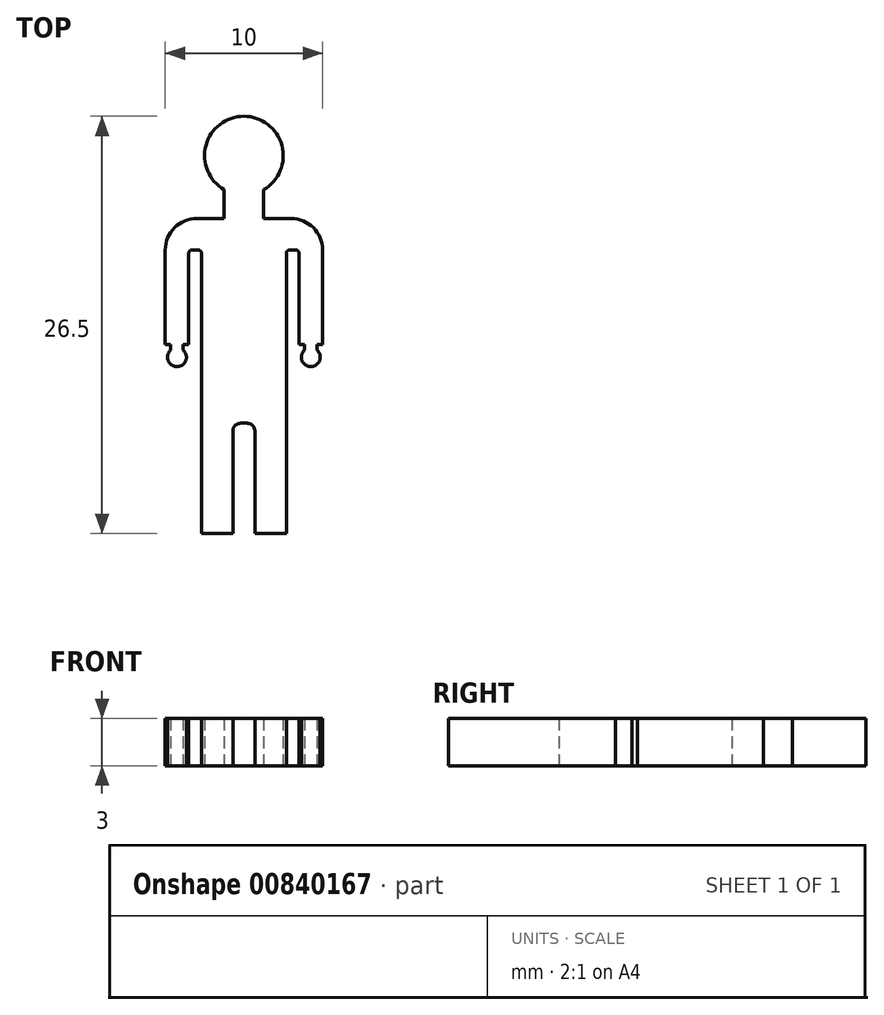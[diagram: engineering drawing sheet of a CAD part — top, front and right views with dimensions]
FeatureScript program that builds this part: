
annotation { "Feature Type Name" : "Feature", "Feature Type Description" : "" }
export const myFeature = defineFeature(function(context is Context, id is Id, definition is map)
    precondition{}
    {
        {
            var Q0;
            Q0=qCreatedBy(makeId("Top.planeOp"),FACE);
            var sketch = newSketch(context, id + "F0", { "sketchPlane" : qUnion([Q0])});
            skArc(sketch, "E0", {"start": v(1.25, -2.17) * mm, "mid": v(0, 2.5) * mm, "end": v(-1.25, -2.17) * mm});
            skLineSegment(sketch, "E1", {"start": v(-1.25, -4) * mm, "end": v(-3, -4) * mm});
            skLineSegment(sketch, "E2", {"start": v(-5, -6) * mm, "end": v(-5, -12) * mm});
            skLineSegment(sketch, "E3", {"start": v(-5, -12) * mm, "end": v(-4.65, -12) * mm});
            skLineSegment(sketch, "E4", {"start": v(-3.5, -12) * mm, "end": v(-3.5, -6.2) * mm});
            skLineSegment(sketch, "E5", {"start": v(-3.3, -6) * mm, "end": v(-2.9, -6) * mm});
            skLineSegment(sketch, "E6", {"start": v(-2.7, -6.2) * mm, "end": v(-2.7, -24) * mm});
            skLineSegment(sketch, "E7", {"start": v(-2.7, -24) * mm, "end": v(-0.7, -24) * mm});
            skLineSegment(sketch, "E8", {"start": v(-0.7, -24) * mm, "end": v(-0.7, -17.5) * mm});
            skLineSegment(sketch, "E9", {"start": v(-0.2, -17) * mm, "end": v(0, -17) * mm});
            skLineSegment(sketch, "E10", {"start": v(0, -4) * mm, "end": v(0, -17) * mm});
            skLineSegment(sketch, "E11.MirrorCS", {"start": v(1.25, -4) * mm, "end": v(3, -4) * mm});
            skLineSegment(sketch, "E12.MirrorCS", {"start": v(5, -6) * mm, "end": v(5, -12) * mm});
            skLineSegment(sketch, "E13.MirrorCS", {"start": v(3.5, -12) * mm, "end": v(3.5, -6.2) * mm});
            skLineSegment(sketch, "E14.MirrorCS", {"start": v(5, -12) * mm, "end": v(4.65, -12) * mm});
            skLineSegment(sketch, "E15.MirrorCS", {"start": v(3.3, -6) * mm, "end": v(2.9, -6) * mm});
            skLineSegment(sketch, "E16.MirrorCS", {"start": v(2.7, -6.2) * mm, "end": v(2.7, -24) * mm});
            skLineSegment(sketch, "E17.MirrorCS", {"start": v(2.7, -24) * mm, "end": v(0.7, -24) * mm});
            skLineSegment(sketch, "E18.MirrorCS", {"start": v(0.2, -17) * mm, "end": v(0, -17) * mm});
            skLineSegment(sketch, "E19.MirrorCS", {"start": v(0.7, -24) * mm, "end": v(0.7, -17.5) * mm});
            skLineSegment(sketch, "E20", {"start": v(-1.25, -4) * mm, "end": v(-1.25, -2.17) * mm});
            skLineSegment(sketch, "E21", {"start": v(1.25, -2.17) * mm, "end": v(1.25, -4) * mm});
            skPoint(sketch, "E22.orphan", {"position": v(0, -4) * mm});
            skPoint(sketch, "E23.visualSharp", {"position": v(-5, -4) * mm});
            skArc(sketch, "E23.filletArc", {"start": v(-3, -4) * mm, "mid": v(-4.41, -4.59) * mm, "end": v(-5, -6) * mm});
            skPoint(sketch, "E24.visualSharp", {"position": v(5, -4) * mm});
            skArc(sketch, "E24.filletArc", {"start": v(5, -6) * mm, "mid": v(4.41, -4.59) * mm, "end": v(3, -4) * mm});
            skPoint(sketch, "E25.visualSharp", {"position": v(-3.5, -6) * mm});
            skArc(sketch, "E25.filletArc", {"start": v(-3.3, -6) * mm, "mid": v(-3.44, -6.06) * mm, "end": v(-3.5, -6.2) * mm});
            skPoint(sketch, "E26.visualSharp", {"position": v(-2.7, -6) * mm});
            skArc(sketch, "E26.filletArc", {"start": v(-2.7, -6.2) * mm, "mid": v(-2.76, -6.06) * mm, "end": v(-2.9, -6) * mm});
            skPoint(sketch, "E27.visualSharp", {"position": v(2.7, -6) * mm});
            skArc(sketch, "E27.filletArc", {"start": v(2.9, -6) * mm, "mid": v(2.76, -6.06) * mm, "end": v(2.7, -6.2) * mm});
            skPoint(sketch, "E28.visualSharp", {"position": v(3.5, -6) * mm});
            skArc(sketch, "E28.filletArc", {"start": v(3.5, -6.2) * mm, "mid": v(3.44, -6.06) * mm, "end": v(3.3, -6) * mm});
            skPoint(sketch, "E29.visualSharp", {"position": v(-0.7, -17) * mm});
            skArc(sketch, "E29.filletArc", {"start": v(-0.2, -17) * mm, "mid": v(-0.55, -17.15) * mm, "end": v(-0.7, -17.5) * mm});
            skPoint(sketch, "E30.visualSharp", {"position": v(0.7, -17) * mm});
            skArc(sketch, "E30.filletArc", {"start": v(0.7, -17.5) * mm, "mid": v(0.55, -17.15) * mm, "end": v(0.2, -17) * mm});
            skArc(sketch, "E31", {"start": v(-4.65, -12.36) * mm, "mid": v(-4.25, -13.4) * mm, "end": v(-3.85, -12.36) * mm});
            skLineSegment(sketch, "E32", {"start": v(-4.65, -12) * mm, "end": v(-4.65, -12.36) * mm});
            skLineSegment(sketch, "E33", {"start": v(-3.85, -12.36) * mm, "end": v(-3.85, -12) * mm});
            skLineSegment(sketch, "E34.trimOffspring", {"start": v(-3.85, -12) * mm, "end": v(-3.5, -12) * mm});
            skArc(sketch, "E35.MirrorCS", {"start": v(4.65, -12.36) * mm, "mid": v(4.25, -13.4) * mm, "end": v(3.85, -12.36) * mm});
            skLineSegment(sketch, "E36.MirrorCS", {"start": v(4.65, -12) * mm, "end": v(4.65, -12.36) * mm});
            skLineSegment(sketch, "E37.MirrorCS", {"start": v(3.85, -12.36) * mm, "end": v(3.85, -12) * mm});
            skLineSegment(sketch, "E38.trimOffspring", {"start": v(3.85, -12) * mm, "end": v(3.5, -12) * mm});
            skSolve(sketch);
        }
        {
            var Q0;
            Q0=makeQuery(id+"F0.imprint","IMPRINT",FACE,{"disambiguationData":[TD([[makeQuery(id+"F0.imprint","IMPRINT",EDGE,{"derivedFrom":sQuery(id+"F0.wireOp",EDGE,"E0")}),1.0]])]});
            extrude(context, id + "F1", {"entities" : qUnion([Q0]), "depth" : 3 * mm, "offsetDistance" : 25 * mm});
        }
    });
